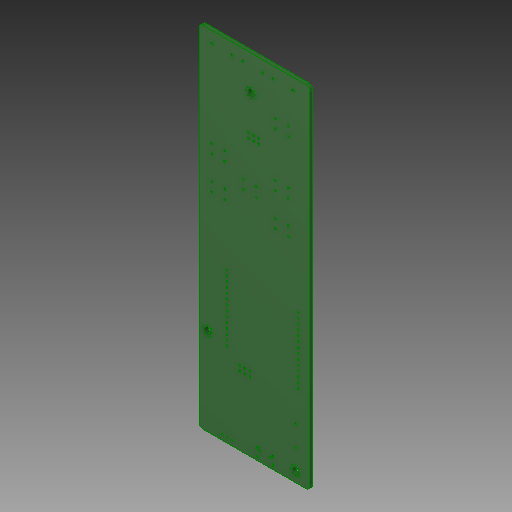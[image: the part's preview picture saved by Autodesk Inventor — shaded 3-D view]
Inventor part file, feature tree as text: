
AUTODESK INVENTOR PART (.ipt)
format: ipt  version: 2019 (Build 230136000, 136)  size: 271,872 bytes
history: native  units: mm
features: extrude x1, sketch x1
ambient origin geometry x8: Origin, YZ Plane, XZ Plane, XY Plane, X Axis, Y Axis, Z Axis, Center Point
bodies: Volumenkörper1 (feature_tree)
feature tree (2):
  extrude  "fantimote.kicad_pcb_Kontur"  [1 undecoded]
  sketch  "Skizze1"  dims[d0=1.6mm d1=0.0mm]
note: 1 required parameter value undecoded (feature->parameter linkage not recoverable at this tier; creation-order binding heuristic only, values carry confidence <= 0.55)
